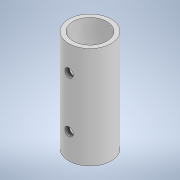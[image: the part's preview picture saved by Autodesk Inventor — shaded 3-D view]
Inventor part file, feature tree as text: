
AUTODESK INVENTOR PART (.ipt)
format: ipt  version: 2022 (Build 260153000, 153)  size: 184,320 bytes
history: native  units: mm
features: extrude x2, sketch x2
ambient origin geometry x8: Origin, YZ Plane, XZ Plane, XY Plane, X Axis, Y Axis, Z Axis, Center Point
bodies: Body1 (feature_tree)
feature tree (4):
  extrude  "Extrusion10"  Depth=8.0mm
  extrude  "Extrusion11"  Depth=6.0mm
  sketch  "Sketch9"  dims[d31=34.456mm d140=8.0mm]
  sketch  "Sketch10"  dims[d141=24.0mm d142=0.0mm d143=6.0mm d144=2.0mm d145=6.0mm d146=2.0mm d147=24.0mm d148=0.0mm d149=10.0mm]
